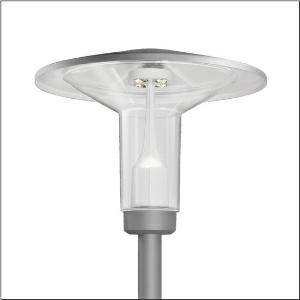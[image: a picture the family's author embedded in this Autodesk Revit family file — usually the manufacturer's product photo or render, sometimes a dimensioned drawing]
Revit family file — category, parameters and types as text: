
# Revit family: laterne_iq___p1_0a_5xa5255ff14h_2151
name_source: partatom
category: Lighting Fixtures
units: mm (PartAtom-declared; Revit-internal decimal feet)

## family parameters
Cut with Voids When Loaded = No
Host = Face
Light Source = No
Part Type = Normal
Room Calculation Point = No
Round Connector Dimension = Use Diameter
Shared = No

## types (1)
- --- (1 x LED, 1510 lm, 10.5 W, 3000K)
    Apparent Load = 11 VA
    CIE Flux Codes = 35 64 91 96 100
    Color Rendering = 70
    Color Temperature = 3000K
    Default Elevation = 1800 mm
    Description = Lantern iQ, mast luminaire, Module 540 iQ-SR, primary light control with 3 zone facetted reflector, of plastic, silver coated, highly specular, structured, primary optical cover: cover, of PMMA, transparent, light distribution: P1.0a, light emission: direct distribution, primary light characteristic: strongly asymmetric, installation type: post-top, LED, High Power LED, rated luminous flux: 1.510lm, luminous efficacy: 144lm/W, light colour: 730, colour temperature: 3000K, control gear: ECG iQ, control: Auto-Match, Temp-Guard, Lumen-Switch, Night-Set, Smart-Wire, Light-Fading, Desk-Remote (wireless, voltage-free reading and setting of iQ features in the workshop via application-optimized NFC function/RFID function), optimised constant luminous flux control (CLO 2.0), Street-Remote, presetting dimming logarithmic, with terminal, 6-pole, max. 2.5mm², mains connection: 230..240V, AC, 50/60Hz, start of lifetime: 11W, end of service life: 11W, reduction: 5W, luminaire housing, upper part, of glass-fibre reinforced polyester, coated, Siteco® metallic grey (DB 702S), diameter: 750mm, height: 583mm, spigot size: d x l = 76 x 70mm (post-top) | with reducer (optional accessory) 60 x 70mm, post-top mast mounting element, of diecast aluminium, coated, Siteco® metallic grey (DB 702S), Module 540 iQ-SR, traffic white (RAL 9016), equipment: standard, protection rating (complete): IP65, insulation class (complete): insulation class II (safety insulation), certification: CE, ENEC, VDE, packaging unit: 1 piece

Light Distribution: P1.0a
    Height = 583 mm
    Lamp = 1 x LED
    Lamp Light Flux = 1510 lm
    Lamp Power = 10.5 W
    Lamp count = 1
    Length = 750 mm
    Luminous efficacy = 144 lm/W
    Manufacturer = Siteco
    ModVariant = No
    Model = 5XA5255FF14H
    Number of Poles = 1
    OnlyDefault = Yes
    Power Factor = 1
    Product Name = Laterne iQ | P1.0a
    Product group = mast luminaire | pylon top
    ProductGroupID = 6100
    Protection Class = Protection class II
    Protection Degree = IP 65
    RLX_Detail_Level = 1
    RLX_Emergency_Light_Flux = 0 lm
    RLX_Emergency_Type = 0
    RLX_Emergency_Type_DB = No
    RlxData = <blob elided: 74045 chars, md5=7ae7b238>
    Socket = socket
    Standby Power = 0 W
    System Light Flux = 1510 lm
    System Power = 11 W
    Type Comments = factory setting: luminous flux: 100 % | dim-lin: 254 | 419 mA
    Type Image = l_1006050.jpg
    URL = http://relux.com
    VarID = @adj_110681
    Voltage = 0 V
    Weight = 0.00 kg
    Width = 0 mm  [stored 0 ft]

note: [stored X ft] marks values corroborated as IEEE doubles in the binary element streams (Revit-internal decimal feet)

## geometry (parser evidence)
native form markers: Blend x4, Sweep x7
no freeform markers — native parametric forms only
